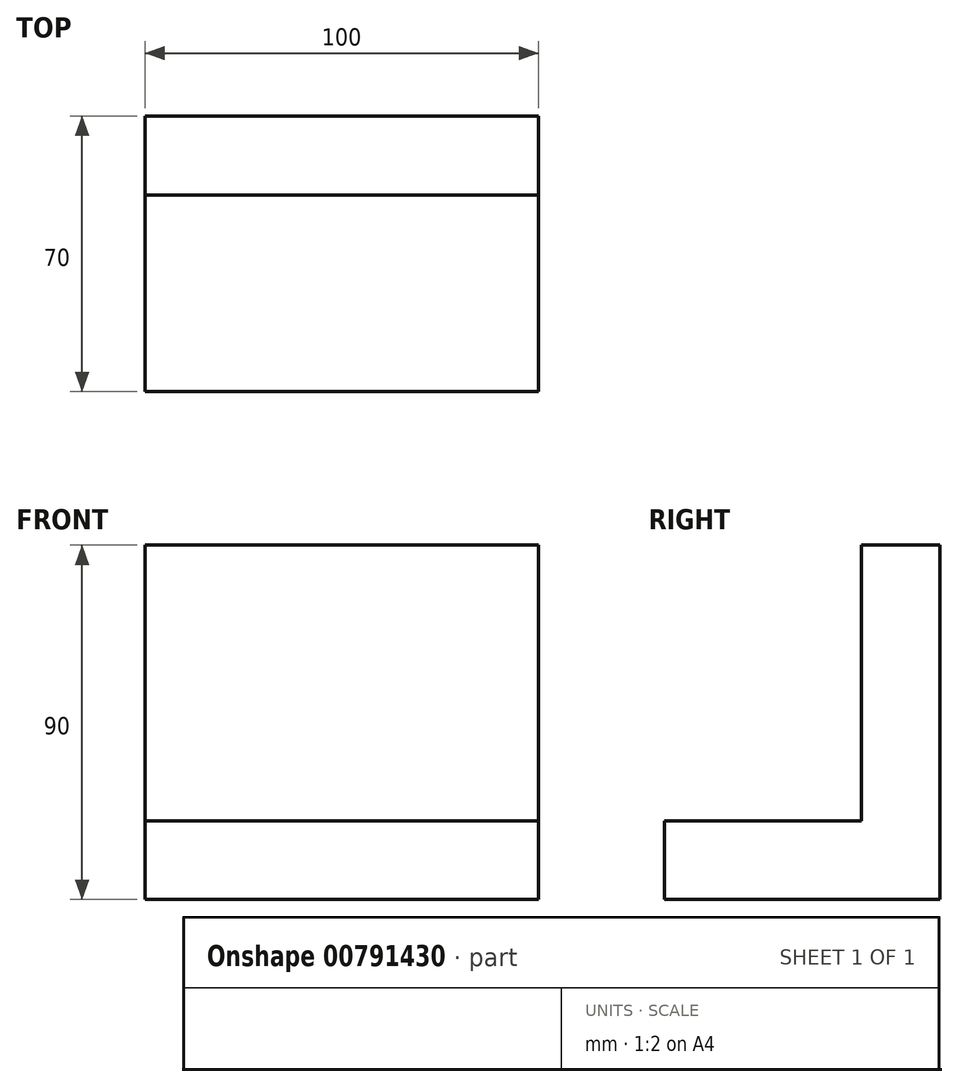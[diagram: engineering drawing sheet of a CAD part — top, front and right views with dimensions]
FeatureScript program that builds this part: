
annotation { "Feature Type Name" : "Feature", "Feature Type Description" : "" }
export const myFeature = defineFeature(function(context is Context, id is Id, definition is map)
    precondition{}
    {
        {
            var Q0;
            Q0=qCreatedBy(makeId("Right.planeOp"),FACE);
            var sketch = newSketch(context, id + "F0", { "sketchPlane" : qUnion([Q0])});
            skLineSegment(sketch, "E0", {"start": v(0, 0) * mm, "end": v(0, 20) * mm});
            skLineSegment(sketch, "E1", {"start": v(0, 20) * mm, "end": v(50, 20) * mm});
            skLineSegment(sketch, "E2", {"start": v(50, 20) * mm, "end": v(50, 90) * mm});
            skLineSegment(sketch, "E3", {"start": v(50, 90) * mm, "end": v(70, 90) * mm});
            skLineSegment(sketch, "E4", {"start": v(70, 90) * mm, "end": v(70, 0) * mm});
            skLineSegment(sketch, "E5", {"start": v(70, 0) * mm, "end": v(0, 0) * mm});
            skSolve(sketch);
        }
        {
            var Q0;
            Q0=makeQuery(id+"F0.imprint","IMPRINT",FACE,{"disambiguationData":[TD([[makeQuery(id+"F0.imprint","IMPRINT",EDGE,{"derivedFrom":sQuery(id+"F0.wireOp",EDGE,"E0")}),-1.0]])]});
            extrude(context, id + "F1", {"entities" : qUnion([Q0]), "depth" : 50 * mm, "offsetDistance" : 25 * mm, "hasSecondDirection" : true, "secondDirectionOppositeDirection" : true, "secondDirectionDepth" : 50 * mm});
        }
    });
